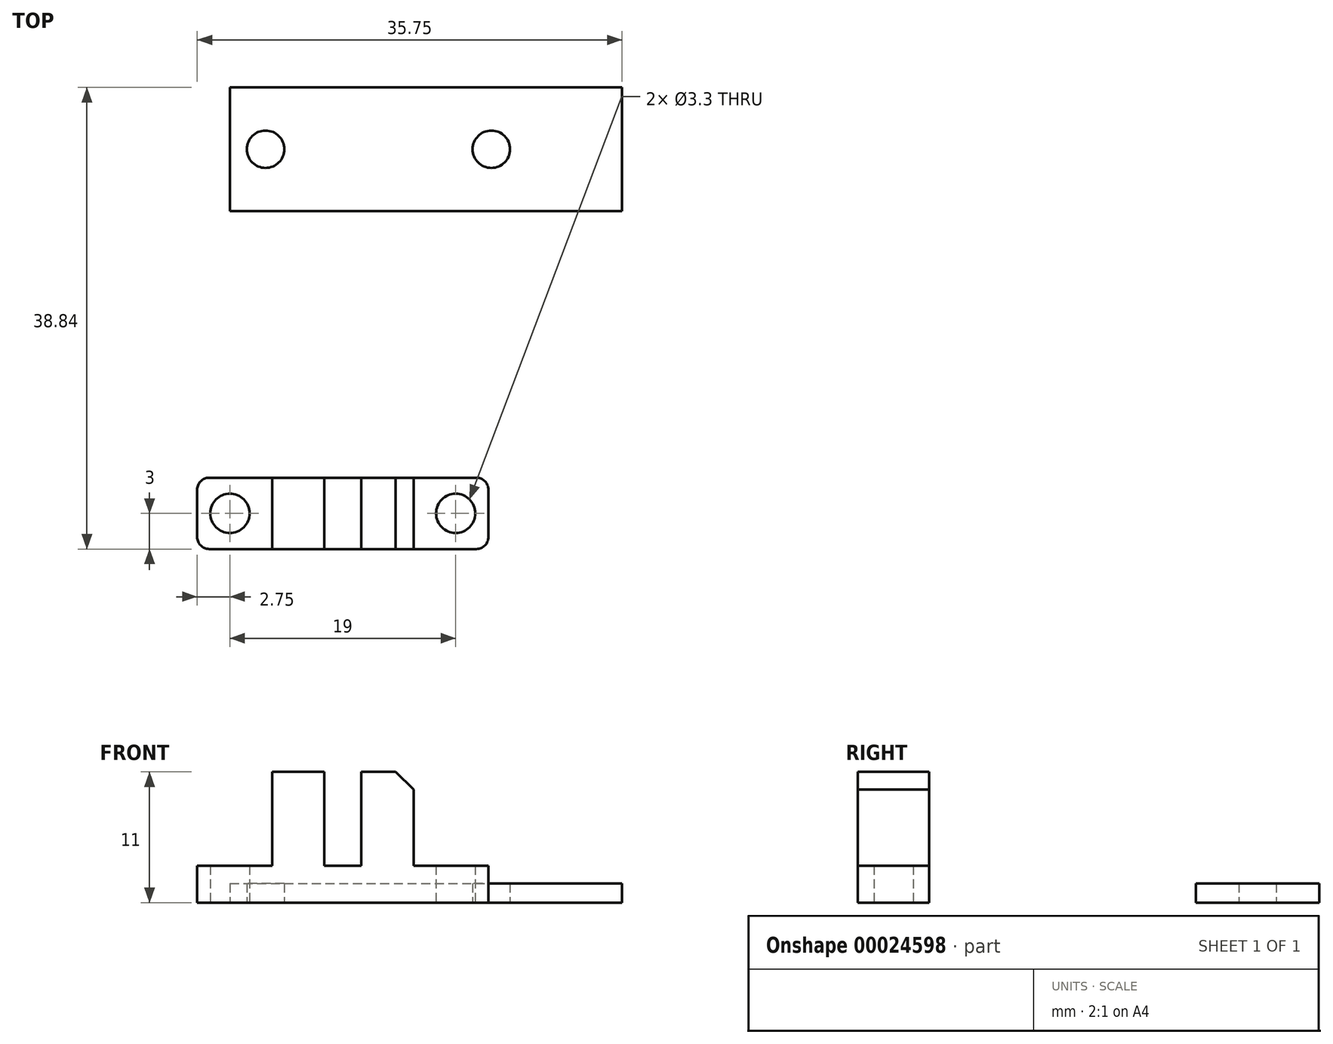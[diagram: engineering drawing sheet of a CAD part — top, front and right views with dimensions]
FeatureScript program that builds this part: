
annotation { "Feature Type Name" : "Feature", "Feature Type Description" : "" }
export const myFeature = defineFeature(function(context is Context, id is Id, definition is map)
    precondition{}
    {
        {
            var Q0;
            Q0=qCreatedBy(makeId("Top.planeOp"),FACE);
            var sketch = newSketch(context, id + "F0", { "sketchPlane" : qUnion([Q0])});
            skLineSegment(sketch, "E0.bottom", {"start": v(0, 5.2) * mm, "end": v(33, 5.2) * mm});
            skLineSegment(sketch, "E0.top", {"start": v(0, -5.2) * mm, "end": v(33, -5.2) * mm});
            skLineSegment(sketch, "E0.left", {"start": v(0, 5.2) * mm, "end": v(0, -5.2) * mm});
            skLineSegment(sketch, "E0.right", {"start": v(33, 5.2) * mm, "end": v(33, -5.2) * mm});
            skLineSegment(sketch, "E1", {"start": v(0, 0) * mm, "end": v(35.47, 0) * mm, "construction": true});
            skCircle(sketch, "E2", {"center": v(3, 0) * mm, "radius": 1.57 * mm});
            skCircle(sketch, "E3", {"center": v(22, 0) * mm, "radius": 1.57 * mm});
            skSolve(sketch);
        }
        {
            var Q0;
            Q0=makeQuery(id+"F0.imprint","IMPRINT",FACE,{"disambiguationData":[TD([[makeQuery(id+"F0.imprint","IMPRINT",EDGE,{"derivedFrom":sQuery(id+"F0.wireOp",EDGE,"E0.bottom")}),-1.0]])]});
            extrude(context, id + "F1", {"entities" : qUnion([Q0]), "depth" : 1.6 * mm});
        }
        {
            var Q0;
            Q0=makeQuery(id+"F1.opExtrude","SWEPT_BODY",BODY,{"disambiguationData":[OSD([sQuery(id+"F0.wireOp",EDGE,"E0.bottom"),sQuery(id+"F0.wireOp",EDGE,"E0.top"),sQuery(id+"F0.wireOp",EDGE,"E0.left"),sQuery(id+"F0.wireOp",EDGE,"E0.right"),sQuery(id+"F0.wireOp",EDGE,"E2"),sQuery(id+"F0.wireOp",EDGE,"E3")])]});
            transform(context, id + "F2", {"entities" : qUnion([Q0]), "transformType" : TransformType.TRANSLATION_3D, "dx" : 0 * mm, "dy" : 30.64 * mm, "dz" : 0 * mm, "makeCopy" : false});
        }
        {
            var Q0;
            Q0=qCreatedBy(makeId("Top.planeOp"),FACE);
            var sketch = newSketch(context, id + "F3", { "sketchPlane" : qUnion([Q0])});
            skLineSegment(sketch, "E4.bottom", {"start": v(-2.75, 3) * mm, "end": v(21.75, 3) * mm});
            skLineSegment(sketch, "E4.top", {"start": v(-2.75, -3) * mm, "end": v(21.75, -3) * mm});
            skLineSegment(sketch, "E4.left", {"start": v(-2.75, 3) * mm, "end": v(-2.75, 0) * mm});
            skLineSegment(sketch, "E4.right", {"start": v(21.75, 3) * mm, "end": v(21.75, 0) * mm});
            skLineSegment(sketch, "E5", {"start": v(-7.47, 0) * mm, "end": v(-2.75, 0) * mm, "construction": true});
            skPoint(sketch, "E6", {"position": v(-2.75, 0) * mm});
            skLineSegment(sketch, "E7", {"start": v(-2.75, 0) * mm, "end": v(-2.75, -3) * mm});
            skCircle(sketch, "E8", {"center": v(0, 0) * mm, "radius": 1.65 * mm});
            skCircle(sketch, "E9", {"center": v(19, 0) * mm, "radius": 1.65 * mm});
            skLineSegment(sketch, "E10", {"start": v(19, 0) * mm, "end": v(21.75, 0) * mm, "construction": true});
            skLineSegment(sketch, "E11", {"start": v(0, 0) * mm, "end": v(9.5, 0) * mm, "construction": true});
            skLineSegment(sketch, "E12", {"start": v(-2.75, 0) * mm, "end": v(0, 0) * mm, "construction": true});
            skLineSegment(sketch, "E13", {"start": v(21.75, 0) * mm, "end": v(21.75, -3) * mm});
            skLineSegment(sketch, "E14", {"start": v(21.75, 0) * mm, "end": v(25.88, 0) * mm, "construction": true});
            skLineSegment(sketch, "E15", {"start": v(9.5, 0) * mm, "end": v(19, 0) * mm, "construction": true});
            skLineSegment(sketch, "E16", {"start": v(9.5, -5.35) * mm, "end": v(9.5, 4.86) * mm, "construction": true});
            skLineSegment(sketch, "E17", {"start": v(7.95, 3) * mm, "end": v(7.95, -3) * mm});
            skLineSegment(sketch, "E18", {"start": v(3.55, 3) * mm, "end": v(3.55, -3) * mm});
            skLineSegment(sketch, "E19", {"start": v(11.05, 3) * mm, "end": v(11.05, -3) * mm});
            skLineSegment(sketch, "E20", {"start": v(15.45, 3) * mm, "end": v(15.45, -3) * mm});
            skSolve(sketch);
        }
        {
            var Q0;
            {var subQ2=sQuery(id+"F3.wireOp",EDGE,"E4.left");Q0=makeQuery(id+"F3.imprint","IMPRINT",FACE,{"disambiguationData":[TD([[makeQuery(id+"F3.imprint","IMPRINT",EDGE,{"derivedFrom":subQ2}),1.0]])]});}
            var Q1;
            {var subQ1=sQuery(id+"F3.wireOp",EDGE,"E17");Q1=makeQuery(id+"F3.imprint","IMPRINT",FACE,{"disambiguationData":[TD([[makeQuery(id+"F3.imprint","IMPRINT",EDGE,{"derivedFrom":subQ1}),1.0]])]});}
            var Q2;
            {var subQ2=sQuery(id+"F3.wireOp",EDGE,"E4.right");Q2=makeQuery(id+"F3.imprint","IMPRINT",FACE,{"disambiguationData":[TD([[makeQuery(id+"F3.imprint","IMPRINT",EDGE,{"derivedFrom":subQ2}),-1.0]])]});}
            var Q3;
            {var subQ1=sQuery(id+"F3.wireOp",EDGE,"E17");Q3=makeQuery(id+"F3.imprint","IMPRINT",FACE,{"disambiguationData":[TD([[makeQuery(id+"F3.imprint","IMPRINT",EDGE,{"derivedFrom":subQ1}),-1.0]])]});}
            var Q4;
            {var subQ0=sQuery(id+"F3.wireOp",EDGE,"E19");Q4=makeQuery(id+"F3.imprint","IMPRINT",FACE,{"disambiguationData":[TD([[makeQuery(id+"F3.imprint","IMPRINT",EDGE,{"derivedFrom":subQ0}),1.0]])]});}
            extrude(context, id + "F4", {"entities" : qUnion([Q0, Q1, Q2, Q3, Q4]), "depth" : 3.1 * mm});
        }
        {
            var Q0;
            {var subQ1=sQuery(id+"F3.wireOp",EDGE,"E17");Q0=makeQuery(id+"F3.imprint","IMPRINT",FACE,{"disambiguationData":[TD([[makeQuery(id+"F3.imprint","IMPRINT",EDGE,{"derivedFrom":subQ1}),-1.0]])]});}
            var Q1;
            {var subQ0=sQuery(id+"F3.wireOp",EDGE,"E19");Q1=makeQuery(id+"F3.imprint","IMPRINT",FACE,{"disambiguationData":[TD([[makeQuery(id+"F3.imprint","IMPRINT",EDGE,{"derivedFrom":subQ0}),1.0]])]});}
            extrude(context, id + "F5", {"entities" : qUnion([Q0, Q1]), "operationType" : NewBodyOperationType.ADD, "depth" : 11 * mm});
        }
        {
            var Q0;
            Q0=makeQuery(id+"F5.opExtrude","CAP_EDGE",EDGE,{"disambiguationData":[OSD([sQuery(id+"F3.wireOp",EDGE,"E20")])],"isStart":false});
            chamfer(context, id + "F6", {"entities" : qUnion([Q0]), "width" : 1.5 * mm, "tangentPropagation" : true});
        }
        {
            var Q0;
            Q0=makeQuery(id+"F4.opExtrude","SWEPT_EDGE",EDGE,{"disambiguationData":[OSD([sQuery(id+"F3.wireOp",EDGE,"E4.top"),sQuery(id+"F3.wireOp",EDGE,"E13")])]});
            var Q1;
            Q1=makeQuery(id+"F4.opExtrude","SWEPT_EDGE",EDGE,{"disambiguationData":[OSD([sQuery(id+"F3.wireOp",EDGE,"E4.bottom"),sQuery(id+"F3.wireOp",EDGE,"E4.right")])]});
            var Q2;
            Q2=makeQuery(id+"F4.opExtrude","SWEPT_EDGE",EDGE,{"disambiguationData":[OSD([sQuery(id+"F3.wireOp",EDGE,"E4.top"),sQuery(id+"F3.wireOp",EDGE,"E7")])]});
            var Q3;
            Q3=makeQuery(id+"F4.opExtrude","SWEPT_EDGE",EDGE,{"disambiguationData":[OSD([sQuery(id+"F3.wireOp",EDGE,"E4.bottom"),sQuery(id+"F3.wireOp",EDGE,"E4.left")])]});
            fillet(context, id + "F7", {"entities" : qUnion([Q0, Q1, Q2, Q3]), "radius" : 1 * mm, "tangentPropagation" : true, "allowEdgeOverflow" : false});
        }
    });
